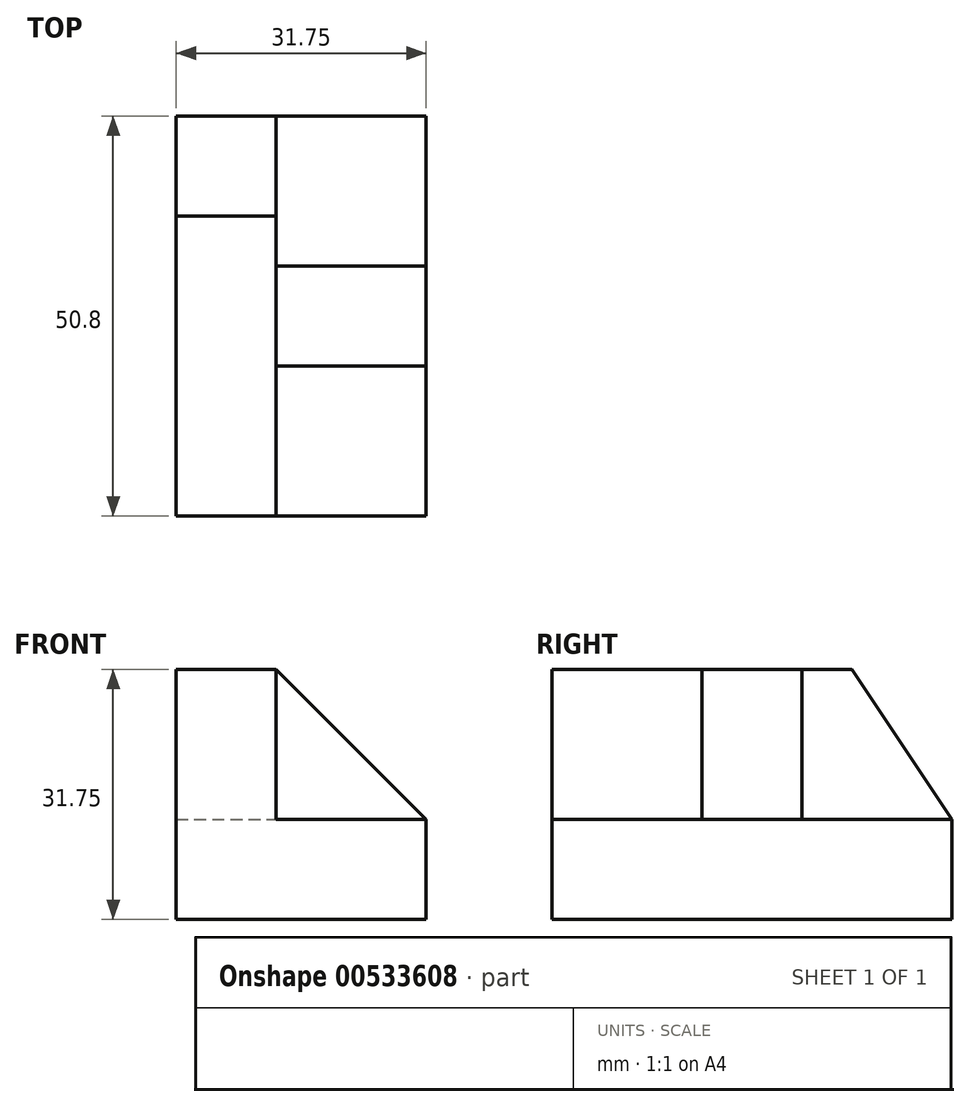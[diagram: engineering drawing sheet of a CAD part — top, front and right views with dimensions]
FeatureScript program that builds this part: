
annotation { "Feature Type Name" : "Feature", "Feature Type Description" : "" }
export const myFeature = defineFeature(function(context is Context, id is Id, definition is map)
    precondition{}
    {
        {
            var Q0;
            Q0=qCreatedBy(makeId("Front.planeOp"),FACE);
            var sketch = newSketch(context, id + "F0", { "sketchPlane" : qUnion([Q0])});
            skLineSegment(sketch, "E0", {"start": v(-64.72, 49.44) * mm, "end": v(-64.72, 17.69) * mm});
            skLineSegment(sketch, "E1", {"start": v(-64.72, 17.69) * mm, "end": v(-32.97, 17.69) * mm});
            skLineSegment(sketch, "E2", {"start": v(-32.97, 17.69) * mm, "end": v(-32.97, 30.39) * mm});
            skLineSegment(sketch, "E3", {"start": v(-32.97, 30.39) * mm, "end": v(-52.02, 30.39) * mm});
            skLineSegment(sketch, "E4", {"start": v(-52.02, 30.39) * mm, "end": v(-52.02, 49.44) * mm});
            skLineSegment(sketch, "E5", {"start": v(-52.02, 49.44) * mm, "end": v(-64.72, 49.44) * mm});
            skSolve(sketch);
        }
        {
            var Q0;
            Q0 = qSketchRegion(id + "F0", true);
            extrude(context, id + "F1", {"entities" : qUnion([Q0]), "depth" : 50.8 * mm, "offsetDistance" : 25.4 * mm});
        }
        {
            var Q0;
            Q0=makeQuery(id+"F1.opExtrude","SWEPT_FACE",FACE,{"disambiguationData":[OSD([sQuery(id+"F0.wireOp",EDGE,"E4")])]});
            var sketch = newSketch(context, id + "F2", { "sketchPlane" : qUnion([Q0])});
            skLineSegment(sketch, "E6", {"start": v(-12.7, 49.44) * mm, "end": v(0, 30.39) * mm});
            skSolve(sketch);
        }
        {
            var Q0;
            Q0 = qSketchRegion(id + "F2", true);
            var Q1;
            {var subQ0=sQuery(id+"F2.wireOp",EDGE,"E6");Q1=makeQuery(id+"F2.imprint","IMPRINT",FACE,{"disambiguationData":[TD([[makeQuery(id+"F2.imprint","IMPRINT",EDGE,{"derivedFrom":subQ0}),1.0]])]});}
            extrude(context, id + "F3", {"entities" : qUnion([Q0, Q1]), "operationType" : NewBodyOperationType.REMOVE, "oppositeDirection" : true, "depth" : 25.4 * mm, "offsetDistance" : 25.4 * mm});
        }
        {
            var Q0;
            Q0=makeQuery(id+"F1.opExtrude","SWEPT_FACE",FACE,{"disambiguationData":[OSD([sQuery(id+"F0.wireOp",EDGE,"E4")])]});
            var sketch = newSketch(context, id + "F4", { "sketchPlane" : qUnion([Q0])});
            skLineSegment(sketch, "E7", {"start": v(-31.75, 49.44) * mm, "end": v(-31.75, 30.39) * mm});
            skLineSegment(sketch, "E8", {"start": v(-31.75, 30.39) * mm, "end": v(-19.05, 30.39) * mm});
            skLineSegment(sketch, "E9", {"start": v(-19.05, 30.39) * mm, "end": v(-19.05, 49.44) * mm});
            skLineSegment(sketch, "E10", {"start": v(-19.05, 49.44) * mm, "end": v(-31.75, 49.44) * mm});
            skSolve(sketch);
        }
        {
            var Q0;
            Q0 = qSketchRegion(id + "F4", true);
            extrude(context, id + "F5", {"entities" : qUnion([Q0]), "operationType" : NewBodyOperationType.ADD, "depth" : 19.05 * mm, "offsetDistance" : 25.4 * mm});
        }
        {
            var Q0;
            Q0=makeQuery(id+"F5.opExtrude","SWEPT_FACE",FACE,{"disambiguationData":[OSD([sQuery(id+"F4.wireOp",EDGE,"E9")])]});
            var sketch = newSketch(context, id + "F6", { "sketchPlane" : qUnion([Q0])});
            skLineSegment(sketch, "E11", {"start": v(52.02, 49.44) * mm, "end": v(32.97, 30.39) * mm});
            skSolve(sketch);
        }
        {
            var Q0;
            Q0 = qSketchRegion(id + "F6", true);
            var Q1;
            Q1=makeQuery(id+"F6.imprint","IMPRINT",FACE,{"disambiguationData":[TD([[makeQuery(id+"F6.imprint","IMPRINT",EDGE,{"derivedFrom":sQuery(id+"F6.wireOp",EDGE,"E11")}),-1.0]])]});
            extrude(context, id + "F7", {"entities" : qUnion([Q0, Q1]), "operationType" : NewBodyOperationType.REMOVE, "endBound" : BoundingType.THROUGH_ALL, "oppositeDirection" : true, "depth" : 25.4 * mm, "offsetDistance" : 25.4 * mm});
        }
    });
